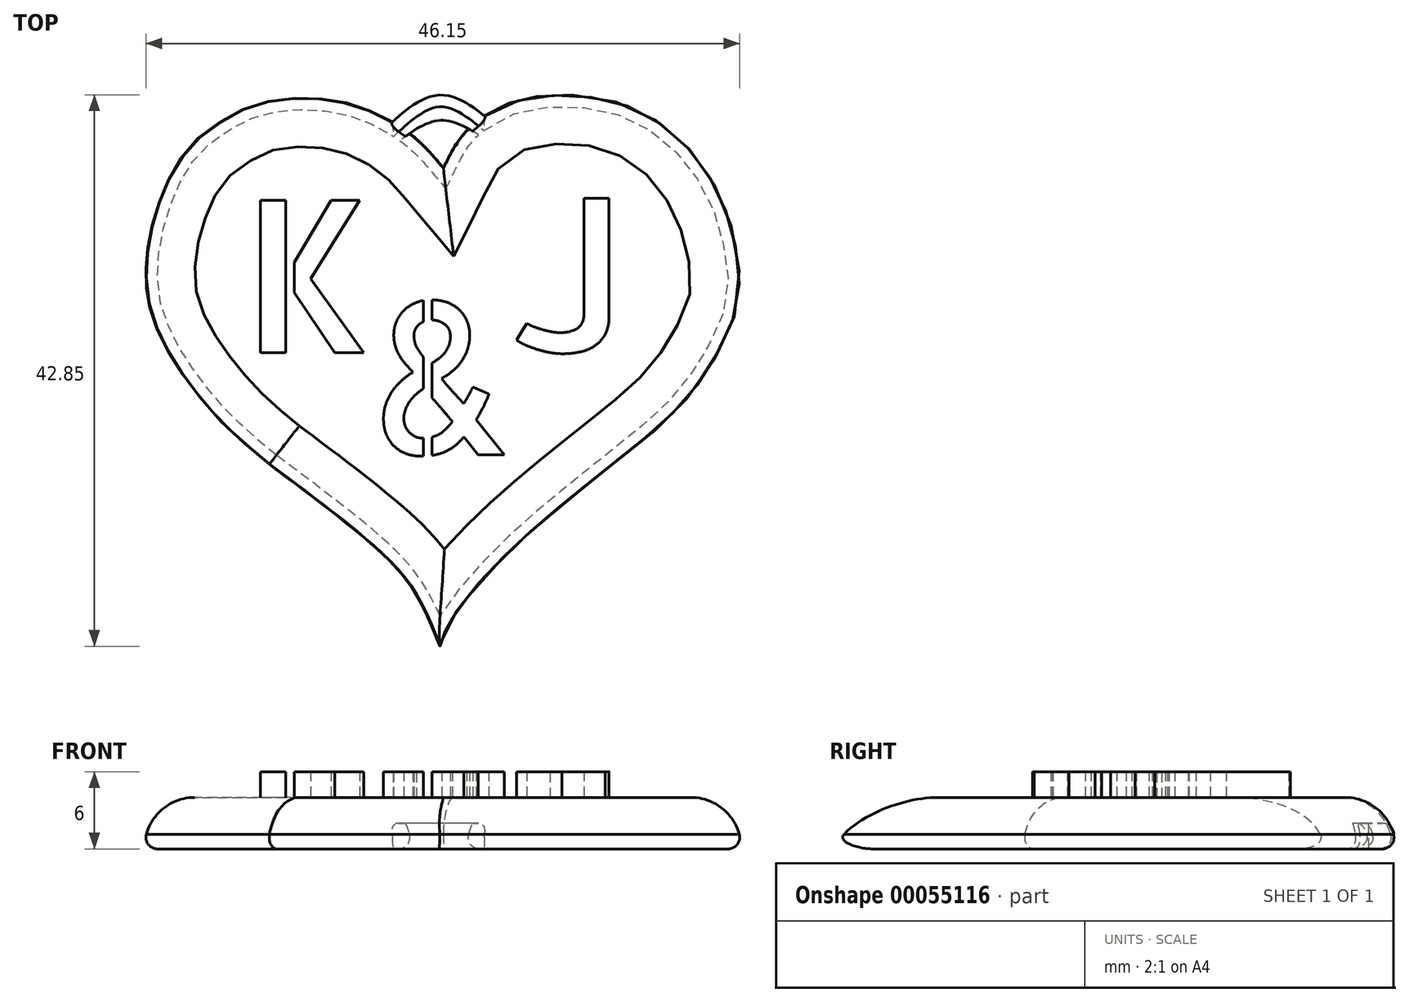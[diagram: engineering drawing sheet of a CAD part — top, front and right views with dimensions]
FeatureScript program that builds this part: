
annotation { "Feature Type Name" : "Feature", "Feature Type Description" : "" }
export const myFeature = defineFeature(function(context is Context, id is Id, definition is map)
    precondition{}
    {
        {
            var Q0;
            Q0=qCreatedBy(makeId("Top.planeOp"),FACE);
            var sketch = newSketch(context, id + "F0", { "sketchPlane" : qUnion([Q0])});
            skFitSpline(sketch, "E0", {"points": [v(15.47, -25.5) * mm, v(13.69, -21.5) * mm, v(10.96, -18.1) * mm, v(2.1, -11.09) * mm], "startDerivative": vector(-6.01, 15.18) * mm, "endDerivative": vector(-22.83, 17.04) * mm});
            skFitSpline(sketch, "E1", {"points": [v(15.47, -25.5) * mm, v(15.86, -24.18) * mm, v(17.3, -21.85) * mm, v(20.14, -18.64) * mm, v(24.42, -14.74) * mm, v(32.14, -8.49) * mm, v(33.77, -6.98) * mm, v(35.68, -4.71) * mm, v(37.45, -1.8) * mm, v(38.57, 0.95) * mm, v(38.84, 3.54) * mm, v(38.4, 6.61) * mm, v(37.54, 9.35) * mm, v(36.27, 11.74) * mm, v(34, 14.49) * mm, v(30.58, 16.76) * mm, v(26.95, 17.7) * mm, v(24, 17.8) * mm, v(21.3, 17.35) * mm, v(18.49, 15.93) * mm, v(16.8, 14.25) * mm, v(15.68, 12.24) * mm], "startDerivative": vector(9.05, 40.9) * mm, "endDerivative": vector(-25.96, -52.25) * mm});
            skFitSpline(sketch, "E2", {"points": [v(2.1, -11.09) * mm, v(-2.08, -7.28) * mm, v(-6.32, -1.25) * mm, v(-7.44, 2.4) * mm, v(-7.5, 4.11) * mm, v(-7.28, 6.43) * mm, v(-6.32, 9.84) * mm, v(-5.16, 12.26) * mm, v(-3.44, 14.4) * mm, v(-1.42, 15.86) * mm, v(0.4, 16.82) * mm, v(2.69, 17.42) * mm, v(4.8, 17.59) * mm, v(7.22, 17.39) * mm, v(9.34, 16.86) * mm, v(11.8, 15.7) * mm, v(13.98, 14.11) * mm, v(15.68, 12.24) * mm], "startDerivative": vector(-50.57, 41.47) * mm, "endDerivative": vector(29.44, -35.3) * mm});
            skSolve(sketch);
        }
        {
            var Q0;
            Q0=qSketchRegion(id+"F0",true);
            extrude(context, id + "F1", {"entities" : qUnion([Q0]), "depth" : 4 * mm});
        }
        {
            var Q0;
            Q0=makeQuery(id+"F1.opExtrude","CAP_EDGE",EDGE,{"disambiguationData":[OSD([sQuery(id+"F0.wireOp",EDGE,"E1")])],"isStart":false});
            var Q1;
            Q1=makeQuery(id+"F1.opExtrude","CAP_EDGE",EDGE,{"disambiguationData":[OSD([sQuery(id+"F0.wireOp",EDGE,"E2")])],"isStart":false});
            var Q2;
            Q2=makeQuery(id+"F1.opExtrude","CAP_EDGE",EDGE,{"disambiguationData":[OSD([sQuery(id+"F0.wireOp",EDGE,"E0")])],"isStart":false});
            fillet(context, id + "F2", {"entities" : qUnion([Q0, Q1, Q2]), "radius" : 3.9 * mm, "tangentPropagation" : true, "allowEdgeOverflow" : false});
        }
        {
            var Q0;
            Q0=makeQuery(id+"F1.opExtrude","CAP_FACE",FACE,{"disambiguationData":[OSD([sQuery(id+"F0.wireOp",EDGE,"E0"),sQuery(id+"F0.wireOp",EDGE,"E1"),sQuery(id+"F0.wireOp",EDGE,"E2")])],"isStart":true});
            fillet(context, id + "F3", {"entities" : qUnion([Q0]), "radius" : 0.9 * mm, "tangentPropagation" : true, "allowEdgeOverflow" : false});
        }
        {
            var Q0;
            Q0=qCreatedBy(makeId("Top.planeOp"),FACE);
            var sketch = newSketch(context, id + "F4", { "sketchPlane" : qUnion([Q0])});
            skText(sketch, "E3", { "text": "K", "fontName": "AllertaStencil-Regular.ttf"});
            skText(sketch, "E4", { "text": "J", "fontName": "AllertaStencil-Regular.ttf"});
            skText(sketch, "E5", { "text": "&", "fontName": "AllertaStencil-Regular.ttf"});
            const initialGuessF4  = {"E3": [0, -0.00233, 1, 0, 0.01185], "E4": [0.02098, -0.00233, 1, 0, 0.01176], "E5": [0.00988, -0.01026, 1, 0, 0.01193]};
            skSetInitialGuess(sketch, initialGuessF4);
            skSolve(sketch);
        }
        {
            var Q0;
            Q0=qSketchRegion(id+"F4",true);
            extrude(context, id + "F5", {"entities" : qUnion([Q0]), "operationType" : NewBodyOperationType.ADD, "depth" : 6 * mm});
        }
        {
            var Q0;
            Q0=qCreatedBy(makeId("Top.planeOp"),FACE);
            var sketch = newSketch(context, id + "F6", { "sketchPlane" : qUnion([Q0])});
            skLineSegment(sketch, "E6", {"start": v(15.64, 12.13) * mm, "end": v(15.64, 12.13) * mm});
            skLineSegment(sketch, "E7", {"start": v(20.1, 15.07) * mm, "end": v(20.1, 15.07) * mm});
            skLineSegment(sketch, "E8", {"start": v(20.1, 15.07) * mm, "end": v(19.13, 14.16) * mm});
            skLineSegment(sketch, "E9", {"start": v(11.75, 13.7) * mm, "end": v(10.64, 14.57) * mm});
            skFitSpline(sketch, "E10", {"points": [v(19.13, 14.16) * mm, v(15.5, 15.73) * mm, v(11.75, 13.7) * mm], "startDerivative": vector(-7.4, 4.95) * mm, "endDerivative": vector(-7.34, -5.78) * mm});
            skFitSpline(sketch, "E11", {"points": [v(20.1, 15.07) * mm, v(15.43, 17.7) * mm, v(10.64, 14.57) * mm], "startDerivative": vector(-9.5, 8.17) * mm, "endDerivative": vector(-9.41, -9.07) * mm});
            skSolve(sketch);
        }
        {
            var Q0;
            Q0=qSketchRegion(id+"F6",true);
            extrude(context, id + "F7", {"entities" : qUnion([Q0]), "operationType" : NewBodyOperationType.ADD, "depth" : 2 * mm});
        }
        {
            var Q0;
            Q0=makeQuery(id+"F7.opExtrude","CAP_EDGE",EDGE,{"disambiguationData":[OSD([sQuery(id+"F6.wireOp",EDGE,"E11")])],"isStart":false});
            var Q1;
            Q1=makeQuery(id+"F7.opExtrude","CAP_EDGE",EDGE,{"disambiguationData":[OSD([sQuery(id+"F6.wireOp",EDGE,"E11")])],"isStart":true});
            fillet(context, id + "F8", {"entities" : qUnion([Q0, Q1]), "radius" : 0.9 * mm, "tangentPropagation" : true, "allowEdgeOverflow" : false});
        }
    });
